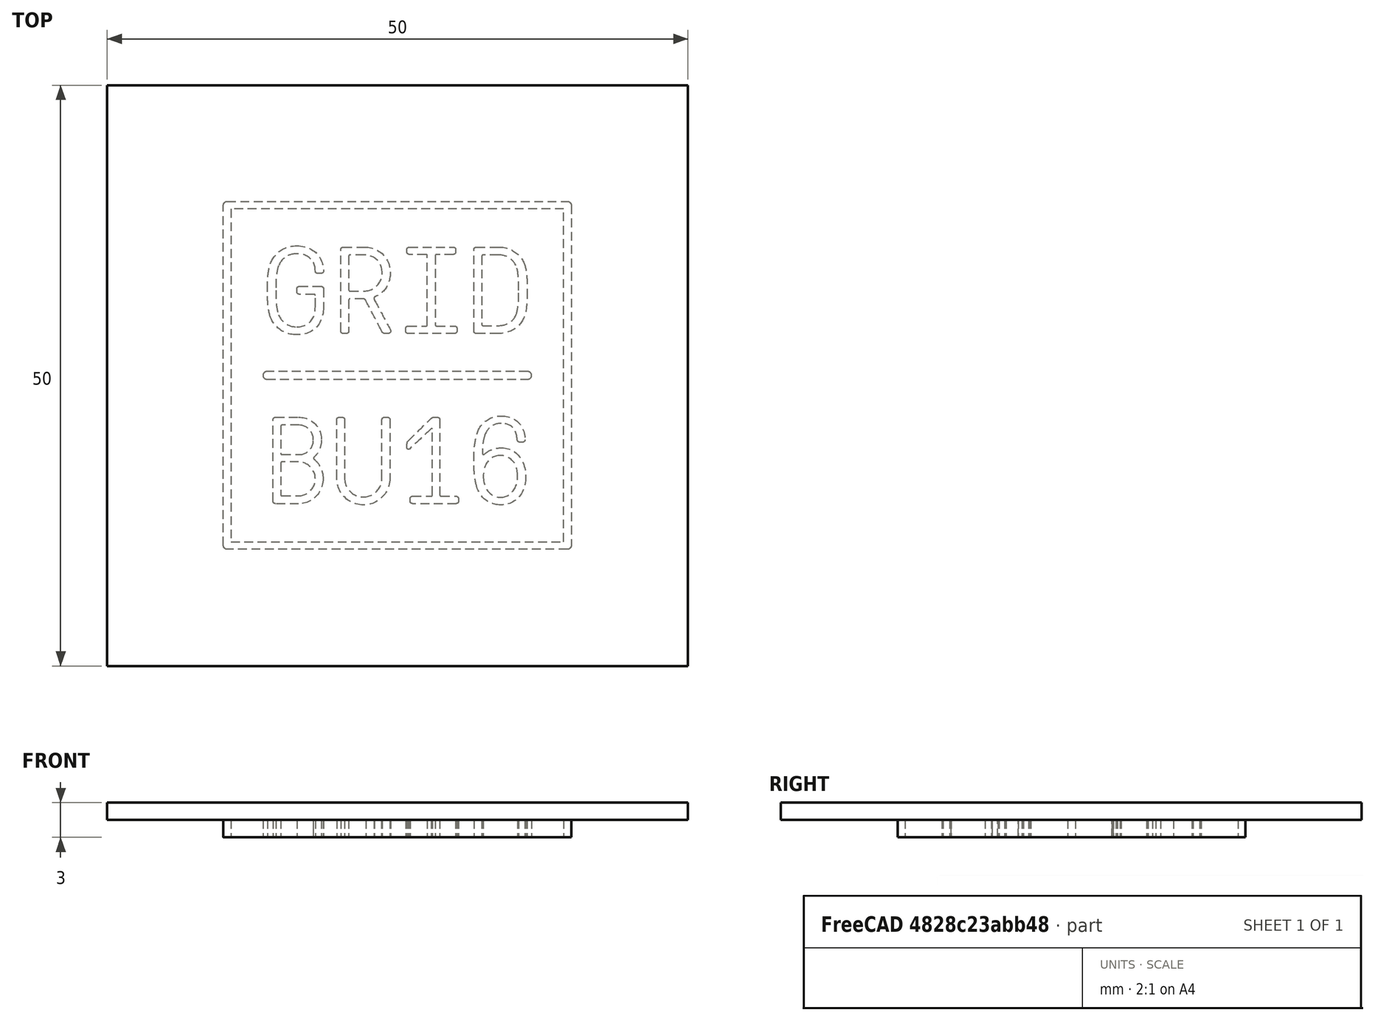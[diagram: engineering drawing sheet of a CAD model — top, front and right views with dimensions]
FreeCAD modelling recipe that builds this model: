
FCSTD DOCUMENT  (FreeCAD 0.18R16131 (Git))
Label: Bu16 Logo 5cm
License: All rights reserved
LicenseURL: http://en.wikipedia.org/wiki/All_rights_reserved
objects: Sketcher::SketchObject×3, PartDesign::Pad×3, PartDesign::Body×1
note: 10 computed .brp shape members not serialized (recipe doc carries the construction recipe); baked Part::Feature solids carry a one-line shape summary decoded from their .brp

FEATURE [Sketcher::SketchObject] Sketch016
  MapMode = 5
  Support = -> [XY_Plane]
  sketch-geometry (12):
    g0: BSplineCurve PolesCount=2 KnotsCount=2 Degree=1 IsPeriodic=0
    g1: BSplineCurve PolesCount=4 KnotsCount=2 Degree=3 IsPeriodic=0
    g2: BSplineCurve PolesCount=2 KnotsCount=2 Degree=1 IsPeriodic=0
    g3: BSplineCurve PolesCount=4 KnotsCount=2 Degree=3 IsPeriodic=0
    g4: BSplineCurve PolesCount=2 KnotsCount=2 Degree=1 IsPeriodic=0
    g5: BSplineCurve PolesCount=4 KnotsCount=2 Degree=3 IsPeriodic=0
    g6: BSplineCurve PolesCount=2 KnotsCount=2 Degree=1 IsPeriodic=0
    g7: BSplineCurve PolesCount=4 KnotsCount=2 Degree=3 IsPeriodic=0
    g8: BSplineCurve PolesCount=2 KnotsCount=2 Degree=1 IsPeriodic=0
    g9: BSplineCurve PolesCount=2 KnotsCount=2 Degree=1 IsPeriodic=0
    g10: BSplineCurve PolesCount=2 KnotsCount=2 Degree=1 IsPeriodic=0
    g11: BSplineCurve PolesCount=2 KnotsCount=2 Degree=1 IsPeriodic=0
  constraints (12):
    c: Coincident(g0,g1)
    c: Coincident(g1,g2)
    c: Coincident(g2,g3)
    c: Coincident(g3,g4)
    c: Coincident(g4,g5)
    c: Coincident(g5,g6)
    c: Coincident(g6,g7)
    c: Coincident(g7,g0)
    c: Coincident(g8,g9)
    c: Coincident(g9,g10)
    c: Coincident(g10,g11)
    c: Coincident(g11,g8)
FEATURE [Sketcher::SketchObject] Sketch
  MapMode = 5
  Support = -> [XY_Plane]
  sketch-geometry (5):
    g0: LineSegment StartX=-25 StartY=25 StartZ=0 EndX=-25 EndY=-25 EndZ=0
    g1: LineSegment StartX=-25 StartY=-25 StartZ=0 EndX=25 EndY=-25 EndZ=0
    g2: LineSegment StartX=25 StartY=-25 StartZ=0 EndX=25 EndY=25 EndZ=0
    g3: LineSegment StartX=25 StartY=25 StartZ=0 EndX=-25 EndY=25 EndZ=0
    g4: Circle [constr] CenterX=0 CenterY=0 CenterZ=0 NormalX=0 NormalY=0 NormalZ=1 AngleXU=0 Radius=35.3553
  constraints (14):
    c: Coincident(g0,g1)
    c: Coincident(g1,g2)
    c: Coincident(g2,g3)
    c: Coincident(g3,g0)
    c: Equal(g0,g1)
    c: Equal(g0,g2)
    c: Equal(g0,g3)
    c: PointOnObject(g0,g4)
    c: PointOnObject(g1,g4)
    c: PointOnObject(g2,g4)
    c: PointOnObject(g3,g4)
    c: Coincident(g4,g-1)
    c: Horizontal(g3)
    c: DistanceX(g3,g3) = 50
FEATURE [PartDesign::Pad] Pad
  Length = 1.5
  Length2 = 100
  Profile = -> Sketch
  Type = 0
FEATURE [Sketcher::SketchObject] Sketch017
  MapMode = 5
  sketch-geometry (178):
    g0: BSplineCurve PolesCount=4 KnotsCount=2 Degree=3 IsPeriodic=0
    g1: BSplineCurve PolesCount=2 KnotsCount=2 Degree=1 IsPeriodic=0
    g2: BSplineCurve PolesCount=4 KnotsCount=2 Degree=3 IsPeriodic=0
    g3: BSplineCurve PolesCount=2 KnotsCount=2 Degree=1 IsPeriodic=0
    g4: BSplineCurve PolesCount=4 KnotsCount=2 Degree=3 IsPeriodic=0
    g5: BSplineCurve PolesCount=2 KnotsCount=2 Degree=1 IsPeriodic=0
    g6: BSplineCurve PolesCount=4 KnotsCount=2 Degree=3 IsPeriodic=0
    g7: BSplineCurve PolesCount=2 KnotsCount=2 Degree=1 IsPeriodic=0
    g8: BSplineCurve PolesCount=4 KnotsCount=2 Degree=3 IsPeriodic=0
    g9: BSplineCurve PolesCount=2 KnotsCount=2 Degree=1 IsPeriodic=0
    g10: BSplineCurve PolesCount=4 KnotsCount=2 Degree=3 IsPeriodic=0
    g11: BSplineCurve PolesCount=4 KnotsCount=2 Degree=3 IsPeriodic=0
    g12: BSplineCurve PolesCount=4 KnotsCount=2 Degree=3 IsPeriodic=0
    g13: BSplineCurve PolesCount=4 KnotsCount=2 Degree=3 IsPeriodic=0
    g14: BSplineCurve PolesCount=4 KnotsCount=2 Degree=3 IsPeriodic=0
    g15: BSplineCurve PolesCount=2 KnotsCount=2 Degree=1 IsPeriodic=0
    g16: BSplineCurve PolesCount=4 KnotsCount=2 Degree=3 IsPeriodic=0
    g17: BSplineCurve PolesCount=4 KnotsCount=2 Degree=3 IsPeriodic=0
    g18: BSplineCurve PolesCount=4 KnotsCount=2 Degree=3 IsPeriodic=0
    g19: BSplineCurve PolesCount=4 KnotsCount=2 Degree=3 IsPeriodic=0
    g20: BSplineCurve PolesCount=4 KnotsCount=2 Degree=3 IsPeriodic=0
    g21: BSplineCurve PolesCount=4 KnotsCount=2 Degree=3 IsPeriodic=0
    g22: BSplineCurve PolesCount=2 KnotsCount=2 Degree=1 IsPeriodic=0
    g23: BSplineCurve PolesCount=4 KnotsCount=2 Degree=3 IsPeriodic=0
    g24: BSplineCurve PolesCount=4 KnotsCount=2 Degree=3 IsPeriodic=0
    g25: BSplineCurve PolesCount=4 KnotsCount=2 Degree=3 IsPeriodic=0
    g26: BSplineCurve PolesCount=4 KnotsCount=2 Degree=3 IsPeriodic=0
    g27: BSplineCurve PolesCount=4 KnotsCount=2 Degree=3 IsPeriodic=0
    g28: BSplineCurve PolesCount=4 KnotsCount=2 Degree=3 IsPeriodic=0
    g29: BSplineCurve PolesCount=4 KnotsCount=2 Degree=3 IsPeriodic=0
    g30: BSplineCurve PolesCount=2 KnotsCount=2 Degree=1 IsPeriodic=0
    g31: BSplineCurve PolesCount=4 KnotsCount=2 Degree=3 IsPeriodic=0
    g32: BSplineCurve PolesCount=2 KnotsCount=2 Degree=1 IsPeriodic=0
    g33: BSplineCurve PolesCount=4 KnotsCount=2 Degree=3 IsPeriodic=0
    g34: BSplineCurve PolesCount=2 KnotsCount=2 Degree=1 IsPeriodic=0
    g35: BSplineCurve PolesCount=4 KnotsCount=2 Degree=3 IsPeriodic=0
    g36: BSplineCurve PolesCount=2 KnotsCount=2 Degree=1 IsPeriodic=0
    g37: BSplineCurve PolesCount=4 KnotsCount=2 Degree=3 IsPeriodic=0
    g38: BSplineCurve PolesCount=2 KnotsCount=2 Degree=1 IsPeriodic=0
    g39: BSplineCurve PolesCount=4 KnotsCount=2 Degree=3 IsPeriodic=0
    g40: BSplineCurve PolesCount=4 KnotsCount=2 Degree=3 IsPeriodic=0
    g41: BSplineCurve PolesCount=2 KnotsCount=2 Degree=1 IsPeriodic=0
    g42: BSplineCurve PolesCount=4 KnotsCount=2 Degree=3 IsPeriodic=0
    g43: BSplineCurve PolesCount=2 KnotsCount=2 Degree=1 IsPeriodic=0
    g44: BSplineCurve PolesCount=4 KnotsCount=2 Degree=3 IsPeriodic=0
    g45: BSplineCurve PolesCount=2 KnotsCount=2 Degree=1 IsPeriodic=0
    g46: BSplineCurve PolesCount=4 KnotsCount=2 Degree=3 IsPeriodic=0
    g47: BSplineCurve PolesCount=2 KnotsCount=2 Degree=1 IsPeriodic=0
    g48: BSplineCurve PolesCount=4 KnotsCount=2 Degree=3 IsPeriodic=0
    g49: BSplineCurve PolesCount=2 KnotsCount=2 Degree=1 IsPeriodic=0
    g50: BSplineCurve PolesCount=4 KnotsCount=2 Degree=3 IsPeriodic=0
    g51: BSplineCurve PolesCount=2 KnotsCount=2 Degree=1 IsPeriodic=0
    g52: BSplineCurve PolesCount=4 KnotsCount=2 Degree=3 IsPeriodic=0
    g53: BSplineCurve PolesCount=2 KnotsCount=2 Degree=1 IsPeriodic=0
    g54: BSplineCurve PolesCount=4 KnotsCount=2 Degree=3 IsPeriodic=0
    g55: BSplineCurve PolesCount=2 KnotsCount=2 Degree=1 IsPeriodic=0
    g56: BSplineCurve PolesCount=4 KnotsCount=2 Degree=3 IsPeriodic=0
    g57: BSplineCurve PolesCount=2 KnotsCount=2 Degree=1 IsPeriodic=0
    g58: BSplineCurve PolesCount=4 KnotsCount=2 Degree=3 IsPeriodic=0
    g59: BSplineCurve PolesCount=2 KnotsCount=2 Degree=1 IsPeriodic=0
    g60: BSplineCurve PolesCount=4 KnotsCount=2 Degree=3 IsPeriodic=0
    g61: BSplineCurve PolesCount=2 KnotsCount=2 Degree=1 IsPeriodic=0
    g62: BSplineCurve PolesCount=4 KnotsCount=2 Degree=3 IsPeriodic=0
    g63: BSplineCurve PolesCount=2 KnotsCount=2 Degree=1 IsPeriodic=0
    g64: BSplineCurve PolesCount=4 KnotsCount=2 Degree=3 IsPeriodic=0
    g65: BSplineCurve PolesCount=2 KnotsCount=2 Degree=1 IsPeriodic=0
    g66: BSplineCurve PolesCount=4 KnotsCount=2 Degree=3 IsPeriodic=0
    g67: BSplineCurve PolesCount=2 KnotsCount=2 Degree=1 IsPeriodic=0
    g68: BSplineCurve PolesCount=4 KnotsCount=2 Degree=3 IsPeriodic=0
    g69: BSplineCurve PolesCount=4 KnotsCount=2 Degree=3 IsPeriodic=0
    g70: BSplineCurve PolesCount=2 KnotsCount=2 Degree=1 IsPeriodic=0
    g71: BSplineCurve PolesCount=4 KnotsCount=2 Degree=3 IsPeriodic=0
    g72: BSplineCurve PolesCount=2 KnotsCount=2 Degree=1 IsPeriodic=0
    g73: BSplineCurve PolesCount=4 KnotsCount=2 Degree=3 IsPeriodic=0
    g74: BSplineCurve PolesCount=2 KnotsCount=2 Degree=1 IsPeriodic=0
    g75: BSplineCurve PolesCount=4 KnotsCount=2 Degree=3 IsPeriodic=0
    g76: BSplineCurve PolesCount=4 KnotsCount=2 Degree=3 IsPeriodic=0
    g77: BSplineCurve PolesCount=4 KnotsCount=2 Degree=3 IsPeriodic=0
    g78: BSplineCurve PolesCount=2 KnotsCount=2 Degree=1 IsPeriodic=0
    g79: BSplineCurve PolesCount=4 KnotsCount=2 Degree=3 IsPeriodic=0
    g80: BSplineCurve PolesCount=2 KnotsCount=2 Degree=1 IsPeriodic=0
    g81: BSplineCurve PolesCount=4 KnotsCount=2 Degree=3 IsPeriodic=0
    g82: BSplineCurve PolesCount=2 KnotsCount=2 Degree=1 IsPeriodic=0
    g83: BSplineCurve PolesCount=4 KnotsCount=2 Degree=3 IsPeriodic=0
    g84: BSplineCurve PolesCount=4 KnotsCount=2 Degree=3 IsPeriodic=0
    g85: BSplineCurve PolesCount=2 KnotsCount=2 Degree=1 IsPeriodic=0
    g86: BSplineCurve PolesCount=4 KnotsCount=2 Degree=3 IsPeriodic=0
    g87: BSplineCurve PolesCount=2 KnotsCount=2 Degree=1 IsPeriodic=0
    g88: BSplineCurve PolesCount=4 KnotsCount=2 Degree=3 IsPeriodic=0
    g89: BSplineCurve PolesCount=2 KnotsCount=2 Degree=1 IsPeriodic=0
    g90: BSplineCurve PolesCount=4 KnotsCount=2 Degree=3 IsPeriodic=0
    g91: BSplineCurve PolesCount=4 KnotsCount=2 Degree=3 IsPeriodic=0
    g92: BSplineCurve PolesCount=4 KnotsCount=2 Degree=3 IsPeriodic=0
    g93: BSplineCurve PolesCount=4 KnotsCount=2 Degree=3 IsPeriodic=0
    g94: BSplineCurve PolesCount=2 KnotsCount=2 Degree=1 IsPeriodic=0
    g95: BSplineCurve PolesCount=4 KnotsCount=2 Degree=3 IsPeriodic=0
    g96: BSplineCurve PolesCount=2 KnotsCount=2 Degree=1 IsPeriodic=0
    g97: BSplineCurve PolesCount=4 KnotsCount=2 Degree=3 IsPeriodic=0
    g98: BSplineCurve PolesCount=2 KnotsCount=2 Degree=1 IsPeriodic=0
    g99: BSplineCurve PolesCount=4 KnotsCount=2 Degree=3 IsPeriodic=0
    g100: BSplineCurve PolesCount=2 KnotsCount=2 Degree=1 IsPeriodic=0
    g101: BSplineCurve PolesCount=4 KnotsCount=2 Degree=3 IsPeriodic=0
    g102: BSplineCurve PolesCount=2 KnotsCount=2 Degree=1 IsPeriodic=0
    g103: BSplineCurve PolesCount=4 KnotsCount=2 Degree=3 IsPeriodic=0
    g104: BSplineCurve PolesCount=4 KnotsCount=2 Degree=3 IsPeriodic=0
    g105: BSplineCurve PolesCount=4 KnotsCount=2 Degree=3 IsPeriodic=0
    g106: BSplineCurve PolesCount=4 KnotsCount=2 Degree=3 IsPeriodic=0
    g107: BSplineCurve PolesCount=2 KnotsCount=2 Degree=1 IsPeriodic=0
    g108: BSplineCurve PolesCount=4 KnotsCount=2 Degree=3 IsPeriodic=0
    g109: BSplineCurve PolesCount=4 KnotsCount=2 Degree=3 IsPeriodic=0
    g110: BSplineCurve PolesCount=2 KnotsCount=2 Degree=1 IsPeriodic=0
    g111: BSplineCurve PolesCount=4 KnotsCount=2 Degree=3 IsPeriodic=0
    g112: BSplineCurve PolesCount=4 KnotsCount=2 Degree=3 IsPeriodic=0
    g113: BSplineCurve PolesCount=2 KnotsCount=2 Degree=1 IsPeriodic=0
    g114: BSplineCurve PolesCount=4 KnotsCount=2 Degree=3 IsPeriodic=0
    g115: BSplineCurve PolesCount=2 KnotsCount=2 Degree=1 IsPeriodic=0
    g116: BSplineCurve PolesCount=4 KnotsCount=2 Degree=3 IsPeriodic=0
    g117: BSplineCurve PolesCount=2 KnotsCount=2 Degree=1 IsPeriodic=0
    g118: BSplineCurve PolesCount=4 KnotsCount=2 Degree=3 IsPeriodic=0
    g119: BSplineCurve PolesCount=4 KnotsCount=2 Degree=3 IsPeriodic=0
    g120: BSplineCurve PolesCount=4 KnotsCount=2 Degree=3 IsPeriodic=0
    g121: BSplineCurve PolesCount=4 KnotsCount=2 Degree=3 IsPeriodic=0
    g122: BSplineCurve PolesCount=2 KnotsCount=2 Degree=1 IsPeriodic=0
    g123: BSplineCurve PolesCount=4 KnotsCount=2 Degree=3 IsPeriodic=0
    g124: BSplineCurve PolesCount=4 KnotsCount=2 Degree=3 IsPeriodic=0
    g125: BSplineCurve PolesCount=2 KnotsCount=2 Degree=1 IsPeriodic=0
    g126: BSplineCurve PolesCount=4 KnotsCount=2 Degree=3 IsPeriodic=0
    g127: BSplineCurve PolesCount=2 KnotsCount=2 Degree=1 IsPeriodic=0
    g128: BSplineCurve PolesCount=4 KnotsCount=2 Degree=3 IsPeriodic=0
    g129: BSplineCurve PolesCount=2 KnotsCount=2 Degree=1 IsPeriodic=0
    g130: BSplineCurve PolesCount=4 KnotsCount=2 Degree=3 IsPeriodic=0
    g131: BSplineCurve PolesCount=2 KnotsCount=2 Degree=1 IsPeriodic=0
    g132: BSplineCurve PolesCount=4 KnotsCount=2 Degree=3 IsPeriodic=0
    g133: BSplineCurve PolesCount=2 KnotsCount=2 Degree=1 IsPeriodic=0
    g134: BSplineCurve PolesCount=4 KnotsCount=2 Degree=3 IsPeriodic=0
    g135: BSplineCurve PolesCount=4 KnotsCount=2 Degree=3 IsPeriodic=0
    g136: BSplineCurve PolesCount=4 KnotsCount=2 Degree=3 IsPeriodic=0
    g137: BSplineCurve PolesCount=4 KnotsCount=2 Degree=3 IsPeriodic=0
    g138: BSplineCurve PolesCount=4 KnotsCount=2 Degree=3 IsPeriodic=0
    g139: BSplineCurve PolesCount=2 KnotsCount=2 Degree=1 IsPeriodic=0
    g140: BSplineCurve PolesCount=4 KnotsCount=2 Degree=3 IsPeriodic=0
    g141: BSplineCurve PolesCount=2 KnotsCount=2 Degree=1 IsPeriodic=0
    g142: BSplineCurve PolesCount=4 KnotsCount=2 Degree=3 IsPeriodic=0
    g143: BSplineCurve PolesCount=2 KnotsCount=2 Degree=1 IsPeriodic=0
    g144: BSplineCurve PolesCount=4 KnotsCount=2 Degree=3 IsPeriodic=0
    g145: BSplineCurve PolesCount=2 KnotsCount=2 Degree=1 IsPeriodic=0
    g146: BSplineCurve PolesCount=4 KnotsCount=2 Degree=3 IsPeriodic=0
    g147: BSplineCurve PolesCount=2 KnotsCount=2 Degree=1 IsPeriodic=0
    g148: BSplineCurve PolesCount=4 KnotsCount=2 Degree=3 IsPeriodic=0
    g149: BSplineCurve PolesCount=2 KnotsCount=2 Degree=1 IsPeriodic=0
    g150: BSplineCurve PolesCount=4 KnotsCount=2 Degree=3 IsPeriodic=0
    g151: BSplineCurve PolesCount=2 KnotsCount=2 Degree=1 IsPeriodic=0
    g152: BSplineCurve PolesCount=4 KnotsCount=2 Degree=3 IsPeriodic=0
    g153: BSplineCurve PolesCount=2 KnotsCount=2 Degree=1 IsPeriodic=0
    g154: BSplineCurve PolesCount=4 KnotsCount=2 Degree=3 IsPeriodic=0
    g155: BSplineCurve PolesCount=2 KnotsCount=2 Degree=1 IsPeriodic=0
    g156: BSplineCurve PolesCount=4 KnotsCount=2 Degree=3 IsPeriodic=0
    g157: BSplineCurve PolesCount=2 KnotsCount=2 Degree=1 IsPeriodic=0
    g158: BSplineCurve PolesCount=4 KnotsCount=2 Degree=3 IsPeriodic=0
    g159: BSplineCurve PolesCount=2 KnotsCount=2 Degree=1 IsPeriodic=0
    g160: BSplineCurve PolesCount=4 KnotsCount=2 Degree=3 IsPeriodic=0
    g161: BSplineCurve PolesCount=2 KnotsCount=2 Degree=1 IsPeriodic=0
    g162: BSplineCurve PolesCount=4 KnotsCount=2 Degree=3 IsPeriodic=0
    g163: BSplineCurve PolesCount=4 KnotsCount=2 Degree=3 IsPeriodic=0
    g164: BSplineCurve PolesCount=4 KnotsCount=2 Degree=3 IsPeriodic=0
    g165: BSplineCurve PolesCount=4 KnotsCount=2 Degree=3 IsPeriodic=0
    g166: BSplineCurve PolesCount=4 KnotsCount=2 Degree=3 IsPeriodic=0
    g167: BSplineCurve PolesCount=4 KnotsCount=2 Degree=3 IsPeriodic=0
    g168: BSplineCurve PolesCount=2 KnotsCount=2 Degree=1 IsPeriodic=0
    g169: BSplineCurve PolesCount=4 KnotsCount=2 Degree=3 IsPeriodic=0
    g170: BSplineCurve PolesCount=4 KnotsCount=2 Degree=3 IsPeriodic=0
    g171: BSplineCurve PolesCount=4 KnotsCount=2 Degree=3 IsPeriodic=0
    g172: BSplineCurve PolesCount=4 KnotsCount=2 Degree=3 IsPeriodic=0
    g173: BSplineCurve PolesCount=4 KnotsCount=2 Degree=3 IsPeriodic=0
    g174: BSplineCurve PolesCount=4 KnotsCount=2 Degree=3 IsPeriodic=0
    g175: BSplineCurve PolesCount=4 KnotsCount=2 Degree=3 IsPeriodic=0
    g176: BSplineCurve PolesCount=4 KnotsCount=2 Degree=3 IsPeriodic=0
    g177: BSplineCurve PolesCount=4 KnotsCount=2 Degree=3 IsPeriodic=0
  constraints (178):
    c: Coincident(g0,g1)
    c: Coincident(g1,g2)
    c: Coincident(g2,g3)
    c: Coincident(g3,g4)
    c: Coincident(g4,g5)
    c: Coincident(g5,g6)
    c: Coincident(g6,g0)
    c: Coincident(g7,g8)
    c: Coincident(g8,g9)
    c: Coincident(g9,g10)
    c: Coincident(g10,g11)
    c: Coincident(g11,g12)
    c: Coincident(g12,g13)
    c: Coincident(g13,g14)
    c: Coincident(g14,g15)
    c: Coincident(g15,g16)
    c: Coincident(g16,g7)
    c: Coincident(g17,g18)
    c: Coincident(g18,g19)
    c: Coincident(g19,g20)
    c: Coincident(g20,g21)
    c: Coincident(g21,g22)
    c: Coincident(g22,g23)
    c: Coincident(g23,g24)
    c: Coincident(g24,g25)
    c: Coincident(g25,g26)
    c: Coincident(g26,g27)
    c: Coincident(g27,g28)
    c: Coincident(g28,g29)
    c: Coincident(g29,g30)
    c: Coincident(g30,g31)
    c: Coincident(g31,g32)
    c: Coincident(g32,g33)
    c: Coincident(g33,g34)
    c: Coincident(g34,g35)
    c: Coincident(g35,g36)
    c: Coincident(g36,g37)
    c: Coincident(g37,g38)
    c: Coincident(g38,g39)
    c: Coincident(g39,g40)
    c: Coincident(g40,g17)
    c: Coincident(g41,g42)
    c: Coincident(g42,g43)
    c: Coincident(g43,g44)
    c: Coincident(g44,g45)
    c: Coincident(g45,g46)
    c: Coincident(g46,g47)
    c: Coincident(g47,g48)
    c: Coincident(g48,g49)
    c: Coincident(g49,g50)
    c: Coincident(g50,g51)
    c: Coincident(g51,g52)
    c: Coincident(g52,g53)
    c: Coincident(g53,g54)
    c: Coincident(g54,g55)
    c: Coincident(g55,g56)
    c: Coincident(g56,g57)
    c: Coincident(g57,g58)
    c: Coincident(g58,g59)
    c: Coincident(g59,g60)
    c: Coincident(g60,g61)
    c: Coincident(g61,g62)
    c: Coincident(g62,g41)
    c: Coincident(g63,g64)
    c: Coincident(g64,g65)
    c: Coincident(g65,g66)
    c: Coincident(g66,g67)
    c: Coincident(g67,g68)
    c: Coincident(g68,g69)
    c: Coincident(g69,g70)
    c: Coincident(g70,g71)
    c: Coincident(g71,g72)
    c: Coincident(g72,g73)
    c: Coincident(g73,g74)
    c: Coincident(g74,g75)
    c: Coincident(g75,g76)
    c: Coincident(g76,g63)
    c: Coincident(g77,g78)
    c: Coincident(g78,g79)
    c: Coincident(g79,g80)
    c: Coincident(g80,g81)
    c: Coincident(g81,g82)
    c: Coincident(g82,g83)
    c: Coincident(g83,g77)
    c: Coincident(g84,g85)
    c: Coincident(g85,g86)
    c: Coincident(g86,g87)
    c: Coincident(g87,g88)
    c: Coincident(g88,g89)
    c: Coincident(g89,g90)
    c: Coincident(g90,g84)
    c: Coincident(g91,g92)
    c: Coincident(g92,g93)
    c: Coincident(g93,g94)
    c: Coincident(g94,g95)
    c: Coincident(g95,g96)
    c: Coincident(g96,g97)
    c: Coincident(g97,g98)
    c: Coincident(g98,g99)
    c: Coincident(g99,g91)
    c: Coincident(g100,g101)
    c: Coincident(g101,g102)
    c: Coincident(g102,g103)
    c: Coincident(g103,g104)
    c: Coincident(g104,g105)
    c: Coincident(g105,g106)
    c: Coincident(g106,g107)
    c: Coincident(g107,g108)
    c: Coincident(g108,g100)
    c: Coincident(g109,g110)
    c: Coincident(g110,g111)
    c: Coincident(g111,g112)
    c: Coincident(g112,g113)
    c: Coincident(g113,g114)
    c: Coincident(g114,g109)
    c: Coincident(g115,g116)
    c: Coincident(g116,g117)
    c: Coincident(g117,g118)
    c: Coincident(g118,g119)
    c: Coincident(g119,g120)
    c: Coincident(g120,g121)
    c: Coincident(g121,g122)
    c: Coincident(g122,g123)
    c: Coincident(g123,g124)
    c: Coincident(g124,g125)
    c: Coincident(g125,g126)
    c: Coincident(g126,g127)
    c: Coincident(g127,g128)
    c: Coincident(g128,g129)
    c: Coincident(g129,g130)
    c: Coincident(g130,g131)
    c: Coincident(g131,g132)
    c: Coincident(g132,g133)
    c: Coincident(g133,g134)
    c: Coincident(g134,g115)
    c: Coincident(g135,g136)
    c: Coincident(g136,g137)
    c: Coincident(g137,g138)
    c: Coincident(g138,g135)
    c: Coincident(g139,g140)
    c: Coincident(g140,g141)
    c: Coincident(g141,g142)
    c: Coincident(g142,g143)
    c: Coincident(g143,g144)
    c: Coincident(g144,g145)
    c: Coincident(g145,g146)
    c: Coincident(g146,g147)
    c: Coincident(g147,g148)
    c: Coincident(g148,g149)
    c: Coincident(g149,g150)
    c: Coincident(g150,g151)
    c: Coincident(g151,g152)
    c: Coincident(g152,g153)
    c: Coincident(g153,g154)
    c: Coincident(g154,g155)
    c: Coincident(g155,g156)
    c: Coincident(g156,g157)
    c: Coincident(g157,g158)
    c: Coincident(g158,g159)
    c: Coincident(g159,g160)
    c: Coincident(g160,g161)
    c: Coincident(g161,g162)
    c: Coincident(g162,g139)
    c: Coincident(g163,g164)
    c: Coincident(g164,g165)
    c: Coincident(g165,g166)
    c: Coincident(g166,g167)
    c: Coincident(g167,g168)
    c: Coincident(g168,g169)
    c: Coincident(g169,g170)
    c: Coincident(g170,g171)
    c: Coincident(g171,g172)
    c: Coincident(g172,g173)
    c: Coincident(g173,g174)
    c: Coincident(g174,g175)
    c: Coincident(g175,g176)
    c: Coincident(g176,g177)
    c: Coincident(g177,g163)
FEATURE [PartDesign::Pad] Pad001
  BaseFeature = -> Pad
  Length = 1.5
  Length2 = 100
  Profile = -> Sketch017
  Reversed = true
  Type = 0
FEATURE [PartDesign::Pad] Pad002
  BaseFeature = -> Pad001
  Length = 1.5
  Length2 = 100
  Profile = -> Sketch016
  Reversed = true
  Type = 0
FEATURE [PartDesign::Body] Body
  Group = -> [Sketch016,Sketch,Pad,Sketch017,Pad001,Pad002]
  Origin = -> Origin
  Tip = -> Pad002
